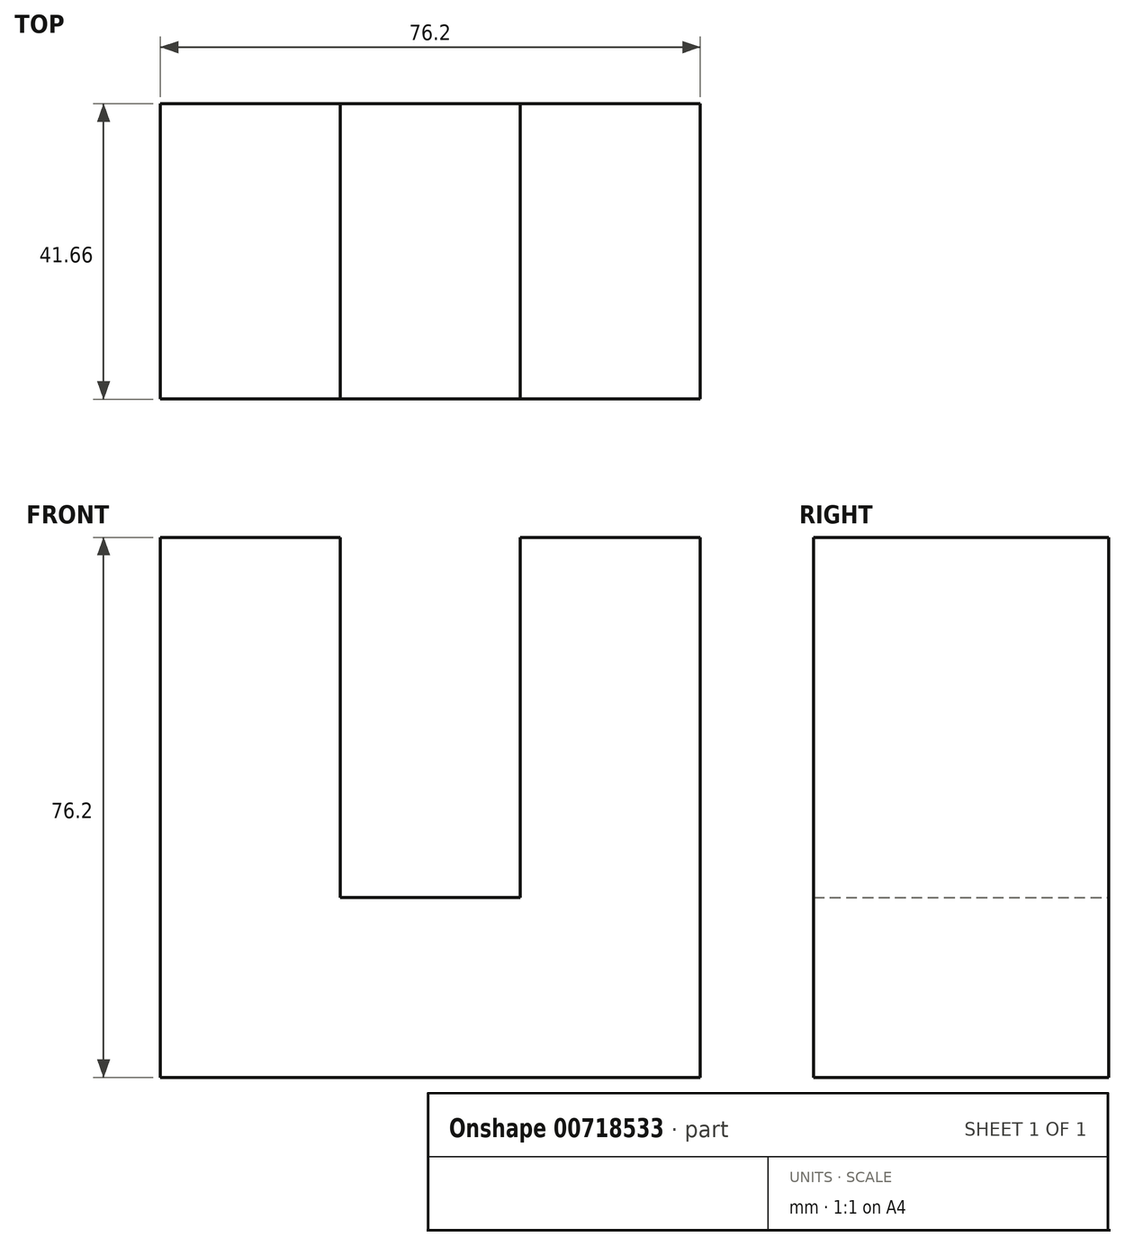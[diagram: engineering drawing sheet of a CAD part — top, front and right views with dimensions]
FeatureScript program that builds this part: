
annotation { "Feature Type Name" : "Feature", "Feature Type Description" : "" }
export const myFeature = defineFeature(function(context is Context, id is Id, definition is map)
    precondition{}
    {
        {
            var Q0;
            Q0=qCreatedBy(makeId("Front.planeOp"),FACE);
            var sketch = newSketch(context, id + "F0", { "sketchPlane" : qUnion([Q0])});
            skLineSegment(sketch, "E0", {"start": v(7.65, 76.2) * mm, "end": v(-17.75, 76.2) * mm});
            skLineSegment(sketch, "E1", {"start": v(-17.75, 76.2) * mm, "end": v(-17.75, 0) * mm});
            skLineSegment(sketch, "E2", {"start": v(-17.75, 0) * mm, "end": v(58.45, 0) * mm});
            skLineSegment(sketch, "E3", {"start": v(58.45, 0) * mm, "end": v(58.45, 76.2) * mm});
            skLineSegment(sketch, "E4", {"start": v(58.45, 76.2) * mm, "end": v(33.05, 76.2) * mm});
            skLineSegment(sketch, "E5", {"start": v(33.05, 76.2) * mm, "end": v(33.05, 25.4) * mm});
            skLineSegment(sketch, "E6", {"start": v(33.05, 25.4) * mm, "end": v(7.65, 25.4) * mm});
            skLineSegment(sketch, "E7", {"start": v(7.65, 25.4) * mm, "end": v(7.65, 76.2) * mm});
            skSolve(sketch);
        }
        {
            var Q0;
            Q0 = qSketchRegion(id + "F0", true);
            extrude(context, id + "F1", {"entities" : qUnion([Q0]), "depth" : 41.66 * mm, "offsetDistance" : 25.4 * mm});
        }
    });
